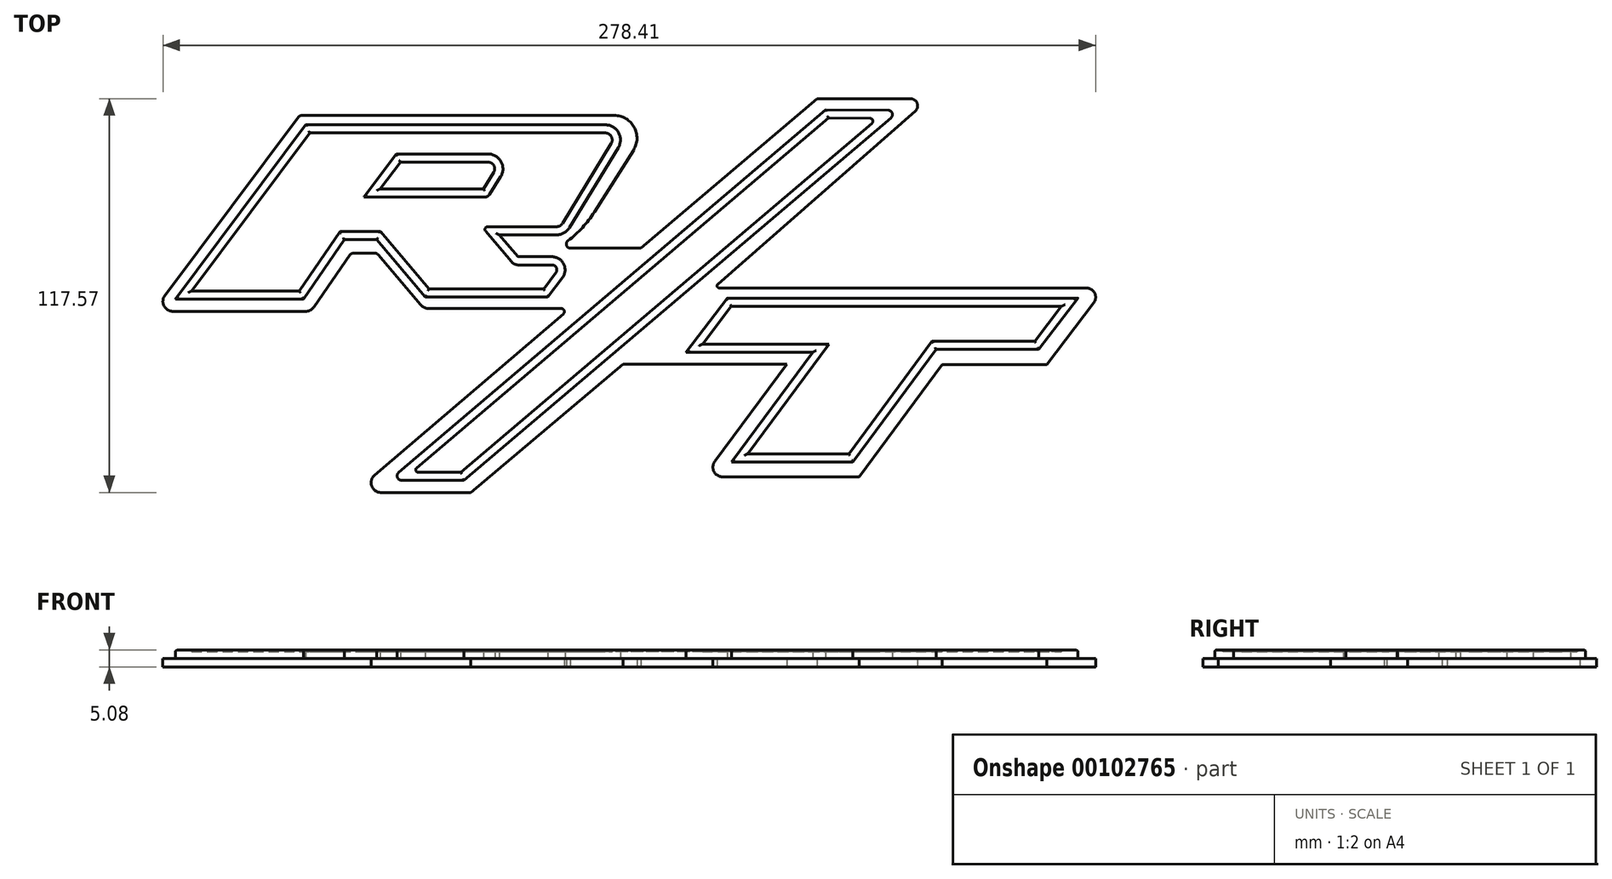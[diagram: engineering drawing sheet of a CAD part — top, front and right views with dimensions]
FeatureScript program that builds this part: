
annotation { "Feature Type Name" : "Feature", "Feature Type Description" : "" }
export const myFeature = defineFeature(function(context is Context, id is Id, definition is map)
    precondition{}
    {
        {
            var Q0;
            Q0=qCreatedBy(makeId("Top.planeOp"),FACE);
            var sketch = newSketch(context, id + "F0", { "sketchPlane" : qUnion([Q0])});
            skLineSegment(sketch, "E0", {"start": v(-246.3, 195.53) * mm, "end": v(-286.16, 142.26) * mm});
            skLineSegment(sketch, "E1", {"start": v(-283.8, 137.55) * mm, "end": v(-244.16, 137.55) * mm});
            skLineSegment(sketch, "E2", {"start": v(-245.29, 196.04) * mm, "end": v(-151.96, 196.04) * mm});
            skLineSegment(sketch, "E3", {"start": v(-144.06, 156.4) * mm, "end": v(-91.53, 201.02) * mm});
            skLineSegment(sketch, "E4", {"start": v(-144.06, 156.4) * mm, "end": v(-165.16, 156.4) * mm});
            skLineSegment(sketch, "E5", {"start": v(-157.95, 167.2) * mm, "end": v(-146.27, 185.71) * mm});
            skLineSegment(sketch, "E6", {"start": v(-241.54, 138.93) * mm, "end": v(-230.95, 154.35) * mm});
            skLineSegment(sketch, "E7", {"start": v(-229.9, 154.9) * mm, "end": v(-223.43, 154.9) * mm});
            skLineSegment(sketch, "E8", {"start": v(-222.46, 154.46) * mm, "end": v(-209.78, 139.5) * mm});
            skLineSegment(sketch, "E9", {"start": v(-207.36, 138.37) * mm, "end": v(-167.79, 138.37) * mm});
            skLineSegment(sketch, "E10", {"start": v(-167.21, 136.8) * mm, "end": v(-223.55, 88.64) * mm});
            skLineSegment(sketch, "E11", {"start": v(-221.64, 83.45) * mm, "end": v(-194.86, 83.45) * mm});
            skLineSegment(sketch, "E12", {"start": v(-194.86, 83.45) * mm, "end": v(-149.4, 121.76) * mm});
            skLineSegment(sketch, "E13", {"start": v(-149.4, 121.76) * mm, "end": v(-100.55, 121.76) * mm});
            skLineSegment(sketch, "E14", {"start": v(-100.55, 121.76) * mm, "end": v(-121.99, 92.77) * mm});
            skLineSegment(sketch, "E15", {"start": v(-119.65, 88.13) * mm, "end": v(-78.87, 88.13) * mm});
            skLineSegment(sketch, "E16", {"start": v(-54.11, 121.61) * mm, "end": v(-78.87, 88.13) * mm});
            skLineSegment(sketch, "E17", {"start": v(-120.7, 144.55) * mm, "end": v(-11.13, 144.55) * mm});
            skLineSegment(sketch, "E18", {"start": v(-121.11, 145.66) * mm, "end": v(-62.16, 197.4) * mm});
            skLineSegment(sketch, "E19", {"start": v(-91.53, 201.02) * mm, "end": v(-63.52, 201.02) * mm});
            skLineSegment(sketch, "E20", {"start": v(-54.11, 121.61) * mm, "end": v(-22.94, 121.61) * mm});
            skLineSegment(sketch, "E21", {"start": v(-22.94, 121.61) * mm, "end": v(-8.9, 140.05) * mm});
            skArc(sketch, "E22", {"start": v(-286.16, 142.26) * mm, "mid": v(-286.43, 139.18) * mm, "end": v(-283.8, 137.55) * mm});
            skPoint(sketch, "E23.visualSharp", {"position": v(-242.48, 137.55) * mm});
            skArc(sketch, "E23.filletArc", {"start": v(-244.16, 137.55) * mm, "mid": v(-242.68, 137.92) * mm, "end": v(-241.54, 138.93) * mm});
            skPoint(sketch, "E24.visualSharp", {"position": v(-230.57, 154.9) * mm});
            skArc(sketch, "E24.filletArc", {"start": v(-229.9, 154.9) * mm, "mid": v(-230.5, 154.76) * mm, "end": v(-230.95, 154.35) * mm});
            skPoint(sketch, "E25.visualSharp", {"position": v(-222.84, 154.9) * mm});
            skArc(sketch, "E25.filletArc", {"start": v(-222.46, 154.46) * mm, "mid": v(-222.9, 154.79) * mm, "end": v(-223.43, 154.9) * mm});
            skPoint(sketch, "E26.visualSharp", {"position": v(-208.83, 138.37) * mm});
            skArc(sketch, "E26.filletArc", {"start": v(-209.78, 139.5) * mm, "mid": v(-208.7, 138.67) * mm, "end": v(-207.36, 138.37) * mm});
            skPoint(sketch, "E27.visualSharp", {"position": v(-245.92, 196.04) * mm});
            skArc(sketch, "E27.filletArc", {"start": v(-245.29, 196.04) * mm, "mid": v(-245.86, 195.9) * mm, "end": v(-246.3, 195.53) * mm});
            skArc(sketch, "E28", {"start": v(-146.27, 185.71) * mm, "mid": v(-146.07, 192.56) * mm, "end": v(-151.96, 196.04) * mm});
            skArc(sketch, "E29", {"start": v(-165.84, 158.64) * mm, "mid": v(-161.5, 162.57) * mm, "end": v(-157.95, 167.2) * mm});
            skArc(sketch, "E30", {"start": v(-165.84, 158.64) * mm, "mid": v(-166.29, 157.28) * mm, "end": v(-165.16, 156.4) * mm});
            skPoint(sketch, "E31.visualSharp", {"position": v(-165.38, 138.37) * mm});
            skArc(sketch, "E31.filletArc", {"start": v(-167.21, 136.8) * mm, "mid": v(-166.96, 137.8) * mm, "end": v(-167.79, 138.37) * mm});
            skPoint(sketch, "E32.visualSharp", {"position": v(-122.38, 144.55) * mm});
            skArc(sketch, "E32.filletArc", {"start": v(-121.11, 145.66) * mm, "mid": v(-121.29, 144.96) * mm, "end": v(-120.7, 144.55) * mm});
            skArc(sketch, "E33", {"start": v(-62.16, 197.4) * mm, "mid": v(-61.58, 199.68) * mm, "end": v(-63.52, 201.02) * mm});
            skArc(sketch, "E34", {"start": v(-223.55, 88.64) * mm, "mid": v(-224.4, 85.38) * mm, "end": v(-221.64, 83.45) * mm});
            skArc(sketch, "E35", {"start": v(-121.99, 92.77) * mm, "mid": v(-122.25, 89.73) * mm, "end": v(-119.65, 88.13) * mm});
            skArc(sketch, "E36", {"start": v(-8.9, 140.05) * mm, "mid": v(-8.62, 142.99) * mm, "end": v(-11.13, 144.55) * mm});
            skSolve(sketch);
        }
        {
            var Q0;
            Q0 = qSketchRegion(id + "F0", true);
            extrude(context, id + "F1", {"entities" : qUnion([Q0]), "depth" : 2.54 * mm});
        }
        {
            var Q0;
            Q0=makeQuery(id+"F1.opExtrude","CAP_FACE",FACE,{"disambiguationData":[OSD([sQuery(id+"F0.wireOp",EDGE,"E0"),sQuery(id+"F0.wireOp",EDGE,"E1"),sQuery(id+"F0.wireOp",EDGE,"E2"),sQuery(id+"F0.wireOp",EDGE,"E3"),sQuery(id+"F0.wireOp",EDGE,"E4"),sQuery(id+"F0.wireOp",EDGE,"E5"),sQuery(id+"F0.wireOp",EDGE,"E6"),sQuery(id+"F0.wireOp",EDGE,"E7"),sQuery(id+"F0.wireOp",EDGE,"E8"),sQuery(id+"F0.wireOp",EDGE,"E9"),sQuery(id+"F0.wireOp",EDGE,"E10"),sQuery(id+"F0.wireOp",EDGE,"E11"),sQuery(id+"F0.wireOp",EDGE,"E12"),sQuery(id+"F0.wireOp",EDGE,"E13"),sQuery(id+"F0.wireOp",EDGE,"E14"),sQuery(id+"F0.wireOp",EDGE,"E15"),sQuery(id+"F0.wireOp",EDGE,"E16"),sQuery(id+"F0.wireOp",EDGE,"E17"),sQuery(id+"F0.wireOp",EDGE,"E18"),sQuery(id+"F0.wireOp",EDGE,"E19"),sQuery(id+"F0.wireOp",EDGE,"E20"),sQuery(id+"F0.wireOp",EDGE,"E21"),sQuery(id+"F0.wireOp",EDGE,"E22"),sQuery(id+"F0.wireOp",EDGE,"E23.filletArc"),sQuery(id+"F0.wireOp",EDGE,"E24.filletArc"),sQuery(id+"F0.wireOp",EDGE,"E25.filletArc"),sQuery(id+"F0.wireOp",EDGE,"E26.filletArc"),sQuery(id+"F0.wireOp",EDGE,"E27.filletArc"),sQuery(id+"F0.wireOp",EDGE,"E28"),sQuery(id+"F0.wireOp",EDGE,"E29"),sQuery(id+"F0.wireOp",EDGE,"E30"),sQuery(id+"F0.wireOp",EDGE,"E31.filletArc"),sQuery(id+"F0.wireOp",EDGE,"E32.filletArc"),sQuery(id+"F0.wireOp",EDGE,"E33"),sQuery(id+"F0.wireOp",EDGE,"E34"),sQuery(id+"F0.wireOp",EDGE,"E35"),sQuery(id+"F0.wireOp",EDGE,"E36")])],"isStart":false});
            var sketch = newSketch(context, id + "F2", { "sketchPlane" : qUnion([Q0])});
            skLineSegment(sketch, "E37", {"start": v(-88.1, 195.27) * mm, "end": v(-211.01, 90.82) * mm});
            skLineSegment(sketch, "E38", {"start": v(-75.1, 193.7) * mm, "end": v(-197.74, 89.49) * mm});
            skLineSegment(sketch, "E39", {"start": v(-197.74, 89.49) * mm, "end": v(-210.52, 89.49) * mm});
            skArc(sketch, "E40", {"start": v(-211.01, 90.82) * mm, "mid": v(-211.23, 89.99) * mm, "end": v(-210.52, 89.49) * mm});
            skLineSegment(sketch, "E41", {"start": v(-88.1, 195.27) * mm, "end": v(-75.64, 195.17) * mm});
            skArc(sketch, "E42", {"start": v(-75.1, 193.7) * mm, "mid": v(-74.86, 194.63) * mm, "end": v(-75.64, 195.17) * mm});
            skLineSegment(sketch, "E43", {"start": v(-117.1, 139.05) * mm, "end": v(-18.52, 139.05) * mm});
            skLineSegment(sketch, "E44", {"start": v(-18.52, 139.05) * mm, "end": v(-26.48, 128.6) * mm});
            skLineSegment(sketch, "E45", {"start": v(-26.48, 128.6) * mm, "end": v(-57.2, 128.6) * mm});
            skLineSegment(sketch, "E46", {"start": v(-57.2, 128.6) * mm, "end": v(-82.01, 95.04) * mm});
            skLineSegment(sketch, "E47", {"start": v(-82.01, 95.04) * mm, "end": v(-112.15, 95.04) * mm});
            skLineSegment(sketch, "E48", {"start": v(-112.15, 95.04) * mm, "end": v(-87.93, 127.8) * mm});
            skLineSegment(sketch, "E49", {"start": v(-87.93, 127.8) * mm, "end": v(-125.67, 127.8) * mm});
            skLineSegment(sketch, "E50", {"start": v(-125.67, 127.8) * mm, "end": v(-117.1, 139.05) * mm});
            skLineSegment(sketch, "E51", {"start": v(-242.87, 190.8) * mm, "end": v(-278.15, 143.66) * mm});
            skLineSegment(sketch, "E52", {"start": v(-242.87, 190.8) * mm, "end": v(-154.67, 190.8) * mm});
            skLineSegment(sketch, "E53", {"start": v(-278.15, 143.66) * mm, "end": v(-246.06, 143.66) * mm});
            skLineSegment(sketch, "E54", {"start": v(-246.06, 143.66) * mm, "end": v(-233.89, 161.39) * mm});
            skLineSegment(sketch, "E55", {"start": v(-233.89, 161.39) * mm, "end": v(-221.81, 161.39) * mm});
            skLineSegment(sketch, "E56", {"start": v(-221.81, 161.39) * mm, "end": v(-207.3, 144.26) * mm});
            skLineSegment(sketch, "E57", {"start": v(-207.3, 144.26) * mm, "end": v(-173.05, 144.26) * mm});
            skLineSegment(sketch, "E58", {"start": v(-173.05, 144.26) * mm, "end": v(-169.43, 149.1) * mm});
            skLineSegment(sketch, "E59", {"start": v(-170.6, 151.42) * mm, "end": v(-180.68, 151.42) * mm});
            skLineSegment(sketch, "E60", {"start": v(-190.42, 161.48) * mm, "end": v(-182.67, 152.34) * mm});
            skLineSegment(sketch, "E61", {"start": v(-189.8, 162.82) * mm, "end": v(-169.3, 162.82) * mm});
            skLineSegment(sketch, "E62", {"start": v(-167.44, 163.86) * mm, "end": v(-152.92, 187.68) * mm});
            skLineSegment(sketch, "E63", {"start": v(-217.09, 184.53) * mm, "end": v(-226.77, 171.7) * mm});
            skLineSegment(sketch, "E64", {"start": v(-217.09, 184.53) * mm, "end": v(-189.65, 184.53) * mm});
            skLineSegment(sketch, "E65", {"start": v(-185.92, 177.78) * mm, "end": v(-189.32, 172.4) * mm});
            skLineSegment(sketch, "E66", {"start": v(-226.77, 171.7) * mm, "end": v(-190.6, 171.7) * mm});
            skArc(sketch, "E67", {"start": v(-185.92, 177.78) * mm, "mid": v(-185.8, 182.26) * mm, "end": v(-189.65, 184.53) * mm});
            skArc(sketch, "E68", {"start": v(-190.6, 171.7) * mm, "mid": v(-189.87, 171.88) * mm, "end": v(-189.32, 172.4) * mm});
            skArc(sketch, "E69", {"start": v(-152.92, 187.68) * mm, "mid": v(-152.88, 189.75) * mm, "end": v(-154.67, 190.8) * mm});
            skArc(sketch, "E70", {"start": v(-169.3, 162.82) * mm, "mid": v(-168.23, 163.1) * mm, "end": v(-167.44, 163.86) * mm});
            skArc(sketch, "E71", {"start": v(-189.8, 162.82) * mm, "mid": v(-190.53, 162.35) * mm, "end": v(-190.42, 161.48) * mm});
            skArc(sketch, "E72", {"start": v(-182.67, 152.34) * mm, "mid": v(-181.78, 151.66) * mm, "end": v(-180.68, 151.42) * mm});
            skArc(sketch, "E73", {"start": v(-169.43, 149.1) * mm, "mid": v(-169.3, 150.62) * mm, "end": v(-170.6, 151.42) * mm});
            skSolve(sketch);
        }
        {
            var Q0;
            Q0 = qSketchRegion(id + "F2", true);
            extrude(context, id + "F3", {"entities" : qUnion([Q0]), "operationType" : NewBodyOperationType.ADD, "depth" : 2.54 * mm});
        }
        {
            var Q0;
            Q0=makeQuery(id+"F1.opExtrude","CAP_FACE",FACE,{"disambiguationData":[OSD([sQuery(id+"F0.wireOp",EDGE,"E0"),sQuery(id+"F0.wireOp",EDGE,"E1"),sQuery(id+"F0.wireOp",EDGE,"E2"),sQuery(id+"F0.wireOp",EDGE,"E3"),sQuery(id+"F0.wireOp",EDGE,"E4"),sQuery(id+"F0.wireOp",EDGE,"E5"),sQuery(id+"F0.wireOp",EDGE,"E6"),sQuery(id+"F0.wireOp",EDGE,"E7"),sQuery(id+"F0.wireOp",EDGE,"E8"),sQuery(id+"F0.wireOp",EDGE,"E9"),sQuery(id+"F0.wireOp",EDGE,"E10"),sQuery(id+"F0.wireOp",EDGE,"E11"),sQuery(id+"F0.wireOp",EDGE,"E12"),sQuery(id+"F0.wireOp",EDGE,"E13"),sQuery(id+"F0.wireOp",EDGE,"E14"),sQuery(id+"F0.wireOp",EDGE,"E15"),sQuery(id+"F0.wireOp",EDGE,"E16"),sQuery(id+"F0.wireOp",EDGE,"E17"),sQuery(id+"F0.wireOp",EDGE,"E18"),sQuery(id+"F0.wireOp",EDGE,"E19"),sQuery(id+"F0.wireOp",EDGE,"E20"),sQuery(id+"F0.wireOp",EDGE,"E21"),sQuery(id+"F0.wireOp",EDGE,"E22"),sQuery(id+"F0.wireOp",EDGE,"E23.filletArc"),sQuery(id+"F0.wireOp",EDGE,"E24.filletArc"),sQuery(id+"F0.wireOp",EDGE,"E25.filletArc"),sQuery(id+"F0.wireOp",EDGE,"E26.filletArc"),sQuery(id+"F0.wireOp",EDGE,"E27.filletArc"),sQuery(id+"F0.wireOp",EDGE,"E28"),sQuery(id+"F0.wireOp",EDGE,"E29"),sQuery(id+"F0.wireOp",EDGE,"E30"),sQuery(id+"F0.wireOp",EDGE,"E31.filletArc"),sQuery(id+"F0.wireOp",EDGE,"E32.filletArc"),sQuery(id+"F0.wireOp",EDGE,"E33"),sQuery(id+"F0.wireOp",EDGE,"E34"),sQuery(id+"F0.wireOp",EDGE,"E35"),sQuery(id+"F0.wireOp",EDGE,"E36")])],"isStart":false});
            var sketch = newSketch(context, id + "F4", { "sketchPlane" : qUnion([Q0])});
            skLineSegment(sketch, "E74.0", {"start": v(-89, 197.7) * mm, "end": v(-216.33, 89.49) * mm});
            skLineSegment(sketch, "E74.2", {"start": v(-69.4, 195.36) * mm, "end": v(-196.84, 87.06) * mm});
            skLineSegment(sketch, "E74.3", {"start": v(-89, 197.7) * mm, "end": v(-70.2, 197.56) * mm});
            skLineSegment(sketch, "E74.4", {"start": v(-196.84, 87.06) * mm, "end": v(-215.44, 87.06) * mm});
            skArc(sketch, "E75", {"start": v(-216.33, 89.49) * mm, "mid": v(-216.74, 87.96) * mm, "end": v(-215.44, 87.06) * mm});
            skPoint(sketch, "E76.orphan", {"position": v(-217.57, 88.44) * mm});
            skArc(sketch, "E77", {"start": v(-69.4, 195.36) * mm, "mid": v(-69.04, 196.74) * mm, "end": v(-70.2, 197.56) * mm});
            skLineSegment(sketch, "E78.0", {"start": v(-130.58, 125.36) * mm, "end": v(-118.3, 141.48) * mm});
            skLineSegment(sketch, "E78.1", {"start": v(-92.75, 125.36) * mm, "end": v(-130.58, 125.36) * mm});
            skLineSegment(sketch, "E78.2", {"start": v(-118.3, 141.48) * mm, "end": v(-13.62, 141.48) * mm});
            skLineSegment(sketch, "E78.3", {"start": v(-116.97, 92.6) * mm, "end": v(-92.75, 125.36) * mm});
            skLineSegment(sketch, "E78.4", {"start": v(-13.62, 141.48) * mm, "end": v(-25.27, 126.17) * mm});
            skLineSegment(sketch, "E78.5", {"start": v(-25.27, 126.17) * mm, "end": v(-55.97, 126.17) * mm});
            skLineSegment(sketch, "E78.6", {"start": v(-55.97, 126.17) * mm, "end": v(-80.79, 92.6) * mm});
            skLineSegment(sketch, "E78.7", {"start": v(-80.79, 92.6) * mm, "end": v(-116.97, 92.6) * mm});
            skLineSegment(sketch, "E79.0", {"start": v(-244.1, 193.24) * mm, "end": v(-283.02, 141.22) * mm});
            skLineSegment(sketch, "E79.1", {"start": v(-283.02, 141.22) * mm, "end": v(-244.78, 141.22) * mm});
            skLineSegment(sketch, "E79.2", {"start": v(-244.78, 141.22) * mm, "end": v(-232.6, 158.95) * mm});
            skLineSegment(sketch, "E79.3", {"start": v(-232.6, 158.95) * mm, "end": v(-222.94, 158.95) * mm});
            skLineSegment(sketch, "E79.4", {"start": v(-222.94, 158.95) * mm, "end": v(-208.43, 141.82) * mm});
            skLineSegment(sketch, "E79.5", {"start": v(-186.29, 160.38) * mm, "end": v(-169.3, 160.38) * mm});
            skArc(sketch, "E79.6", {"start": v(-169.3, 160.38) * mm, "mid": v(-167.03, 160.97) * mm, "end": v(-165.35, 162.6) * mm});
            skLineSegment(sketch, "E79.7", {"start": v(-165.35, 162.6) * mm, "end": v(-150.84, 186.41) * mm});
            skArc(sketch, "E79.8", {"start": v(-150.84, 186.41) * mm, "mid": v(-150.75, 190.95) * mm, "end": v(-154.67, 193.24) * mm});
            skLineSegment(sketch, "E79.9", {"start": v(-186.29, 160.38) * mm, "end": v(-180.8, 153.91) * mm});
            skArc(sketch, "E79.10", {"start": v(-180.8, 153.91) * mm, "mid": v(-180.75, 153.87) * mm, "end": v(-180.68, 153.86) * mm});
            skLineSegment(sketch, "E79.11", {"start": v(-170.6, 153.86) * mm, "end": v(-180.68, 153.86) * mm});
            skArc(sketch, "E79.12", {"start": v(-167.48, 147.64) * mm, "mid": v(-167.12, 151.7) * mm, "end": v(-170.6, 153.86) * mm});
            skLineSegment(sketch, "E79.13", {"start": v(-171.83, 141.82) * mm, "end": v(-167.48, 147.64) * mm});
            skLineSegment(sketch, "E79.14", {"start": v(-244.1, 193.24) * mm, "end": v(-154.67, 193.24) * mm});
            skLineSegment(sketch, "E79.15", {"start": v(-208.43, 141.82) * mm, "end": v(-171.83, 141.82) * mm});
            skLineSegment(sketch, "E80.0", {"start": v(-215.87, 182.1) * mm, "end": v(-189.65, 182.1) * mm});
            skLineSegment(sketch, "E80.1", {"start": v(-215.87, 182.1) * mm, "end": v(-221.88, 174.13) * mm});
            skLineSegment(sketch, "E80.2", {"start": v(-221.88, 174.13) * mm, "end": v(-191.1, 174.13) * mm});
            skLineSegment(sketch, "E80.3", {"start": v(-187.99, 179.08) * mm, "end": v(-191.1, 174.13) * mm});
            skArc(sketch, "E81.0", {"start": v(-187.99, 179.08) * mm, "mid": v(-187.93, 181.08) * mm, "end": v(-189.65, 182.1) * mm});
            skSolve(sketch);
        }
        {
            var Q0;
            Q0 = qSketchRegion(id + "F4", true);
            extrude(context, id + "F5", {"entities" : qUnion([Q0]), "operationType" : NewBodyOperationType.ADD, "depth" : 2.54 * mm});
        }
        {
            var Q0;
            Q0=makeQuery(id+"F5.boolean.opBoolean","MERGE",FACE,{"derivedFrom":[makeQuery(id+"F3.opExtrude","CAP_FACE",FACE,{"disambiguationData":[OSD([sQuery(id+"F2.wireOp",EDGE,"E51"),sQuery(id+"F2.wireOp",EDGE,"E52"),sQuery(id+"F2.wireOp",EDGE,"E53"),sQuery(id+"F2.wireOp",EDGE,"E54"),sQuery(id+"F2.wireOp",EDGE,"E55"),sQuery(id+"F2.wireOp",EDGE,"E56"),sQuery(id+"F2.wireOp",EDGE,"E57"),sQuery(id+"F2.wireOp",EDGE,"E58"),sQuery(id+"F2.wireOp",EDGE,"E59"),sQuery(id+"F2.wireOp",EDGE,"E60"),sQuery(id+"F2.wireOp",EDGE,"E61"),sQuery(id+"F2.wireOp",EDGE,"E62"),sQuery(id+"F2.wireOp",EDGE,"E63"),sQuery(id+"F2.wireOp",EDGE,"E64"),sQuery(id+"F2.wireOp",EDGE,"E65"),sQuery(id+"F2.wireOp",EDGE,"E66"),sQuery(id+"F2.wireOp",EDGE,"E67"),sQuery(id+"F2.wireOp",EDGE,"E68"),sQuery(id+"F2.wireOp",EDGE,"E69"),sQuery(id+"F2.wireOp",EDGE,"E70"),sQuery(id+"F2.wireOp",EDGE,"E71"),sQuery(id+"F2.wireOp",EDGE,"E72"),sQuery(id+"F2.wireOp",EDGE,"E73")])],"isStart":false}),makeQuery(id+"F5.opExtrude","CAP_FACE",FACE,{"disambiguationData":[OSD([sQuery(id+"F4.wireOp",EDGE,"E79.0"),sQuery(id+"F4.wireOp",EDGE,"E79.1"),sQuery(id+"F4.wireOp",EDGE,"E79.2"),sQuery(id+"F4.wireOp",EDGE,"E79.3"),sQuery(id+"F4.wireOp",EDGE,"E79.4"),sQuery(id+"F4.wireOp",EDGE,"E79.5"),sQuery(id+"F4.wireOp",EDGE,"E79.6"),sQuery(id+"F4.wireOp",EDGE,"E79.7"),sQuery(id+"F4.wireOp",EDGE,"E79.8"),sQuery(id+"F4.wireOp",EDGE,"E79.9"),sQuery(id+"F4.wireOp",EDGE,"E79.10"),sQuery(id+"F4.wireOp",EDGE,"E79.11"),sQuery(id+"F4.wireOp",EDGE,"E79.12"),sQuery(id+"F4.wireOp",EDGE,"E79.13"),sQuery(id+"F4.wireOp",EDGE,"E79.14"),sQuery(id+"F4.wireOp",EDGE,"E79.15"),sQuery(id+"F4.wireOp",EDGE,"E80.0"),sQuery(id+"F4.wireOp",EDGE,"E80.1"),sQuery(id+"F4.wireOp",EDGE,"E80.2"),sQuery(id+"F4.wireOp",EDGE,"E80.3"),sQuery(id+"F4.wireOp",EDGE,"E81.0")])],"isStart":false})]});
            var sketch = newSketch(context, id + "F6", { "sketchPlane" : qUnion([Q0])});
            skLineSegment(sketch, "E82.0", {"start": v(-189.8, 162.82) * mm, "end": v(-169.3, 162.82) * mm});
            skLineSegment(sketch, "E82.1", {"start": v(-190.42, 161.48) * mm, "end": v(-182.67, 152.34) * mm});
            skPoint(sketch, "E82.2", {"position": v(-189.8, 162) * mm});
            skArc(sketch, "E82.3", {"start": v(-189.8, 162.82) * mm, "mid": v(-190.53, 162.35) * mm, "end": v(-190.42, 161.48) * mm});
            skArc(sketch, "E82.4", {"start": v(-182.67, 152.34) * mm, "mid": v(-181.78, 151.66) * mm, "end": v(-180.68, 151.42) * mm});
            skLineSegment(sketch, "E82.5", {"start": v(-170.6, 151.42) * mm, "end": v(-180.68, 151.42) * mm});
            skArc(sketch, "E82.6", {"start": v(-169.43, 149.1) * mm, "mid": v(-169.3, 150.62) * mm, "end": v(-170.6, 151.42) * mm});
            skLineSegment(sketch, "E82.7", {"start": v(-173.05, 144.26) * mm, "end": v(-169.43, 149.1) * mm});
            skLineSegment(sketch, "E83.0", {"start": v(-207.3, 144.26) * mm, "end": v(-173.05, 144.26) * mm});
            skLineSegment(sketch, "E84.0", {"start": v(-221.81, 161.39) * mm, "end": v(-207.3, 144.26) * mm});
            skLineSegment(sketch, "E85.0", {"start": v(-233.89, 161.39) * mm, "end": v(-221.81, 161.39) * mm});
            skLineSegment(sketch, "E86.0", {"start": v(-246.06, 143.66) * mm, "end": v(-233.89, 161.39) * mm});
            skLineSegment(sketch, "E87.0", {"start": v(-278.15, 143.66) * mm, "end": v(-246.06, 143.66) * mm});
            skLineSegment(sketch, "E88.0", {"start": v(-242.87, 190.8) * mm, "end": v(-278.15, 143.66) * mm});
            skArc(sketch, "E89.0", {"start": v(-169.3, 162.82) * mm, "mid": v(-168.23, 163.1) * mm, "end": v(-167.44, 163.86) * mm});
            skLineSegment(sketch, "E89.1", {"start": v(-167.44, 163.86) * mm, "end": v(-152.92, 187.68) * mm});
            skArc(sketch, "E89.2", {"start": v(-152.92, 187.68) * mm, "mid": v(-152.88, 189.75) * mm, "end": v(-154.67, 190.8) * mm});
            skLineSegment(sketch, "E89.3", {"start": v(-242.87, 190.8) * mm, "end": v(-154.67, 190.8) * mm});
            skLineSegment(sketch, "E89.4", {"start": v(-217.09, 184.53) * mm, "end": v(-189.65, 184.53) * mm});
            skLineSegment(sketch, "E89.5", {"start": v(-217.09, 184.53) * mm, "end": v(-226.77, 171.7) * mm});
            skLineSegment(sketch, "E89.6", {"start": v(-226.77, 171.7) * mm, "end": v(-190.6, 171.7) * mm});
            skArc(sketch, "E89.7", {"start": v(-185.92, 177.78) * mm, "mid": v(-185.8, 182.26) * mm, "end": v(-189.65, 184.53) * mm});
            skLineSegment(sketch, "E89.8", {"start": v(-185.92, 177.78) * mm, "end": v(-189.32, 172.4) * mm});
            skArc(sketch, "E89.9", {"start": v(-190.6, 171.7) * mm, "mid": v(-189.87, 171.88) * mm, "end": v(-189.32, 172.4) * mm});
            skLineSegment(sketch, "E90.0", {"start": v(-75.1, 193.7) * mm, "end": v(-197.74, 89.49) * mm});
            skLineSegment(sketch, "E91.0", {"start": v(-197.74, 89.49) * mm, "end": v(-210.52, 89.49) * mm});
            skArc(sketch, "E92.1", {"start": v(-211.01, 90.82) * mm, "mid": v(-211.23, 89.99) * mm, "end": v(-210.52, 89.49) * mm});
            skLineSegment(sketch, "E93.0.0", {"start": v(-70.2, 197.56) * mm, "end": v(-89, 197.7) * mm});
            skLineSegment(sketch, "E93.0.3", {"start": v(-215.44, 87.06) * mm, "end": v(-196.84, 87.06) * mm});
            skArc(sketch, "E94.0.5", {"start": v(-69.4, 195.36) * mm, "mid": v(-69.04, 196.74) * mm, "end": v(-70.2, 197.56) * mm});
            skLineSegment(sketch, "E95.0", {"start": v(-88.1, 195.27) * mm, "end": v(-211.01, 90.82) * mm});
            skLineSegment(sketch, "E96.0", {"start": v(-88.1, 195.27) * mm, "end": v(-75.64, 195.17) * mm});
            skArc(sketch, "E97.0", {"start": v(-75.1, 193.7) * mm, "mid": v(-74.86, 194.63) * mm, "end": v(-75.64, 195.17) * mm});
            skPoint(sketch, "E93.0.1.end.orphan", {"position": v(-216.33, 89.49) * mm});
            skLineSegment(sketch, "E98.0", {"start": v(-117.1, 139.05) * mm, "end": v(-18.52, 139.05) * mm});
            skLineSegment(sketch, "E98.1", {"start": v(-125.67, 127.8) * mm, "end": v(-117.1, 139.05) * mm});
            skLineSegment(sketch, "E98.2", {"start": v(-87.93, 127.8) * mm, "end": v(-125.67, 127.8) * mm});
            skLineSegment(sketch, "E98.3", {"start": v(-112.15, 95.04) * mm, "end": v(-87.93, 127.8) * mm});
            skLineSegment(sketch, "E98.4", {"start": v(-82.01, 95.04) * mm, "end": v(-112.15, 95.04) * mm});
            skLineSegment(sketch, "E98.5", {"start": v(-57.2, 128.6) * mm, "end": v(-82.01, 95.04) * mm});
            skLineSegment(sketch, "E99.0", {"start": v(-18.52, 139.05) * mm, "end": v(-26.48, 128.6) * mm});
            skLineSegment(sketch, "E99.1", {"start": v(-26.48, 128.6) * mm, "end": v(-57.2, 128.6) * mm});
            skSolve(sketch);
        }
        {
            var Q0;
            Q0 = qSketchRegion(id + "F6", true);
            extrude(context, id + "F9", {"entities" : qUnion([Q0]), "operationType" : NewBodyOperationType.REMOVE, "oppositeDirection" : true, "depth" : 0.5 * mm});
        }
        {
            var Q0;
            {var subQ0=sQuery(id+"F4.wireOp",EDGE,"E79.10");var subQ1=sQuery(id+"F4.wireOp",EDGE,"E79.0");var subQ2=sQuery(id+"F4.wireOp",EDGE,"E79.15");var subQ3=sQuery(id+"F4.wireOp",EDGE,"E79.12");var subQ4=sQuery(id+"F4.wireOp",EDGE,"E79.14");var subQ5=sQuery(id+"F4.wireOp",EDGE,"E79.11");var subQ6=sQuery(id+"F4.wireOp",EDGE,"E79.9");var subQ7=sQuery(id+"F4.wireOp",EDGE,"E79.13");var subQ8=sQuery(id+"F4.wireOp",EDGE,"E79.2");var subQ9=sQuery(id+"F4.wireOp",EDGE,"E79.3");var subQ10=sQuery(id+"F4.wireOp",EDGE,"E79.5");var subQ11=sQuery(id+"F4.wireOp",EDGE,"E79.1");var subQ12=sQuery(id+"F4.wireOp",EDGE,"E79.4");var subQ13=sQuery(id+"F4.wireOp",EDGE,"E79.8");var subQ14=sQuery(id+"F4.wireOp",EDGE,"E79.6");var subQ15=sQuery(id+"F4.wireOp",EDGE,"E79.7");Q0=makeQuery(id+"F9.boolean.opBoolean","SPLIT",FACE,{"disambiguationData":[TD([makeQuery(id+"F5.opExtrude","SWEPT_FACE",FACE,{"disambiguationData":[OSD([subQ1])]})])],"derivedFrom":makeQuery(id+"F5.boolean.opBoolean","MERGE",FACE,{"derivedFrom":[makeQuery(id+"F3.opExtrude","CAP_FACE",FACE,{"disambiguationData":[OSD([sQuery(id+"F2.wireOp",EDGE,"E51"),sQuery(id+"F2.wireOp",EDGE,"E52"),sQuery(id+"F2.wireOp",EDGE,"E53"),sQuery(id+"F2.wireOp",EDGE,"E54"),sQuery(id+"F2.wireOp",EDGE,"E55"),sQuery(id+"F2.wireOp",EDGE,"E56"),sQuery(id+"F2.wireOp",EDGE,"E57"),sQuery(id+"F2.wireOp",EDGE,"E58"),sQuery(id+"F2.wireOp",EDGE,"E59"),sQuery(id+"F2.wireOp",EDGE,"E60"),sQuery(id+"F2.wireOp",EDGE,"E61"),sQuery(id+"F2.wireOp",EDGE,"E62"),sQuery(id+"F2.wireOp",EDGE,"E63"),sQuery(id+"F2.wireOp",EDGE,"E64"),sQuery(id+"F2.wireOp",EDGE,"E65"),sQuery(id+"F2.wireOp",EDGE,"E66"),sQuery(id+"F2.wireOp",EDGE,"E67"),sQuery(id+"F2.wireOp",EDGE,"E68"),sQuery(id+"F2.wireOp",EDGE,"E69"),sQuery(id+"F2.wireOp",EDGE,"E70"),sQuery(id+"F2.wireOp",EDGE,"E71"),sQuery(id+"F2.wireOp",EDGE,"E72"),sQuery(id+"F2.wireOp",EDGE,"E73")])],"isStart":false}),makeQuery(id+"F5.opExtrude","CAP_FACE",FACE,{"disambiguationData":[OSD([subQ1,subQ11,subQ8,subQ9,subQ12,subQ10,subQ14,subQ15,subQ13,subQ6,subQ0,subQ5,subQ3,subQ7,subQ4,subQ2,sQuery(id+"F4.wireOp",EDGE,"E80.0"),sQuery(id+"F4.wireOp",EDGE,"E80.1"),sQuery(id+"F4.wireOp",EDGE,"E80.2"),sQuery(id+"F4.wireOp",EDGE,"E80.3"),sQuery(id+"F4.wireOp",EDGE,"E81.0")])],"isStart":false})]})});}
            var Q1;
            Q1=makeQuery(id+"F5.boolean.opBoolean","MERGE",FACE,{"derivedFrom":[makeQuery(id+"F3.opExtrude","CAP_FACE",FACE,{"disambiguationData":[OSD([sQuery(id+"F2.wireOp",EDGE,"E37"),sQuery(id+"F2.wireOp",EDGE,"E38"),sQuery(id+"F2.wireOp",EDGE,"E39"),sQuery(id+"F2.wireOp",EDGE,"E40"),sQuery(id+"F2.wireOp",EDGE,"E41"),sQuery(id+"F2.wireOp",EDGE,"E42")])],"isStart":false}),makeQuery(id+"F5.opExtrude","CAP_FACE",FACE,{"disambiguationData":[OSD([sQuery(id+"F4.wireOp",EDGE,"E74.0"),sQuery(id+"F4.wireOp",EDGE,"E74.2"),sQuery(id+"F4.wireOp",EDGE,"E74.3"),sQuery(id+"F4.wireOp",EDGE,"E74.4"),sQuery(id+"F4.wireOp",EDGE,"E75"),sQuery(id+"F4.wireOp",EDGE,"E77")])],"isStart":false})]});
            var Q2;
            Q2=makeQuery(id+"F5.boolean.opBoolean","MERGE",FACE,{"derivedFrom":[makeQuery(id+"F3.opExtrude","CAP_FACE",FACE,{"disambiguationData":[OSD([sQuery(id+"F2.wireOp",EDGE,"E43"),sQuery(id+"F2.wireOp",EDGE,"E44"),sQuery(id+"F2.wireOp",EDGE,"E45"),sQuery(id+"F2.wireOp",EDGE,"E46"),sQuery(id+"F2.wireOp",EDGE,"E47"),sQuery(id+"F2.wireOp",EDGE,"E48"),sQuery(id+"F2.wireOp",EDGE,"E49"),sQuery(id+"F2.wireOp",EDGE,"E50")])],"isStart":false}),makeQuery(id+"F5.opExtrude","CAP_FACE",FACE,{"disambiguationData":[OSD([sQuery(id+"F4.wireOp",EDGE,"E78.0"),sQuery(id+"F4.wireOp",EDGE,"E78.1"),sQuery(id+"F4.wireOp",EDGE,"E78.2"),sQuery(id+"F4.wireOp",EDGE,"E78.3"),sQuery(id+"F4.wireOp",EDGE,"E78.4"),sQuery(id+"F4.wireOp",EDGE,"E78.5"),sQuery(id+"F4.wireOp",EDGE,"E78.6"),sQuery(id+"F4.wireOp",EDGE,"E78.7")])],"isStart":false})]});
            var Q3;
            {var subQ0=sQuery(id+"F4.wireOp",EDGE,"E81.0");var subQ1=sQuery(id+"F4.wireOp",EDGE,"E80.2");var subQ2=sQuery(id+"F4.wireOp",EDGE,"E80.0");var subQ3=sQuery(id+"F4.wireOp",EDGE,"E80.1");var subQ4=sQuery(id+"F4.wireOp",EDGE,"E80.3");Q3=makeQuery(id+"F9.boolean.opBoolean","SPLIT",FACE,{"disambiguationData":[TD([makeQuery(id+"F5.opExtrude","SWEPT_FACE",FACE,{"disambiguationData":[OSD([subQ2])]})])],"derivedFrom":makeQuery(id+"F5.boolean.opBoolean","MERGE",FACE,{"derivedFrom":[makeQuery(id+"F3.opExtrude","CAP_FACE",FACE,{"disambiguationData":[OSD([sQuery(id+"F2.wireOp",EDGE,"E51"),sQuery(id+"F2.wireOp",EDGE,"E52"),sQuery(id+"F2.wireOp",EDGE,"E53"),sQuery(id+"F2.wireOp",EDGE,"E54"),sQuery(id+"F2.wireOp",EDGE,"E55"),sQuery(id+"F2.wireOp",EDGE,"E56"),sQuery(id+"F2.wireOp",EDGE,"E57"),sQuery(id+"F2.wireOp",EDGE,"E58"),sQuery(id+"F2.wireOp",EDGE,"E59"),sQuery(id+"F2.wireOp",EDGE,"E60"),sQuery(id+"F2.wireOp",EDGE,"E61"),sQuery(id+"F2.wireOp",EDGE,"E62"),sQuery(id+"F2.wireOp",EDGE,"E63"),sQuery(id+"F2.wireOp",EDGE,"E64"),sQuery(id+"F2.wireOp",EDGE,"E65"),sQuery(id+"F2.wireOp",EDGE,"E66"),sQuery(id+"F2.wireOp",EDGE,"E67"),sQuery(id+"F2.wireOp",EDGE,"E68"),sQuery(id+"F2.wireOp",EDGE,"E69"),sQuery(id+"F2.wireOp",EDGE,"E70"),sQuery(id+"F2.wireOp",EDGE,"E71"),sQuery(id+"F2.wireOp",EDGE,"E72"),sQuery(id+"F2.wireOp",EDGE,"E73")])],"isStart":false}),makeQuery(id+"F5.opExtrude","CAP_FACE",FACE,{"disambiguationData":[OSD([sQuery(id+"F4.wireOp",EDGE,"E79.0"),sQuery(id+"F4.wireOp",EDGE,"E79.1"),sQuery(id+"F4.wireOp",EDGE,"E79.2"),sQuery(id+"F4.wireOp",EDGE,"E79.3"),sQuery(id+"F4.wireOp",EDGE,"E79.4"),sQuery(id+"F4.wireOp",EDGE,"E79.5"),sQuery(id+"F4.wireOp",EDGE,"E79.6"),sQuery(id+"F4.wireOp",EDGE,"E79.7"),sQuery(id+"F4.wireOp",EDGE,"E79.8"),sQuery(id+"F4.wireOp",EDGE,"E79.9"),sQuery(id+"F4.wireOp",EDGE,"E79.10"),sQuery(id+"F4.wireOp",EDGE,"E79.11"),sQuery(id+"F4.wireOp",EDGE,"E79.12"),sQuery(id+"F4.wireOp",EDGE,"E79.13"),sQuery(id+"F4.wireOp",EDGE,"E79.14"),sQuery(id+"F4.wireOp",EDGE,"E79.15"),subQ2,subQ3,subQ1,subQ4,subQ0])],"isStart":false})]})});}
            fillet(context, id + "F7", {"entities" : qUnion([Q0, Q1, Q2, Q3]), "radius" : 0.5 * mm, "tangentPropagation" : true, "allowEdgeOverflow" : false});
        }
    });
